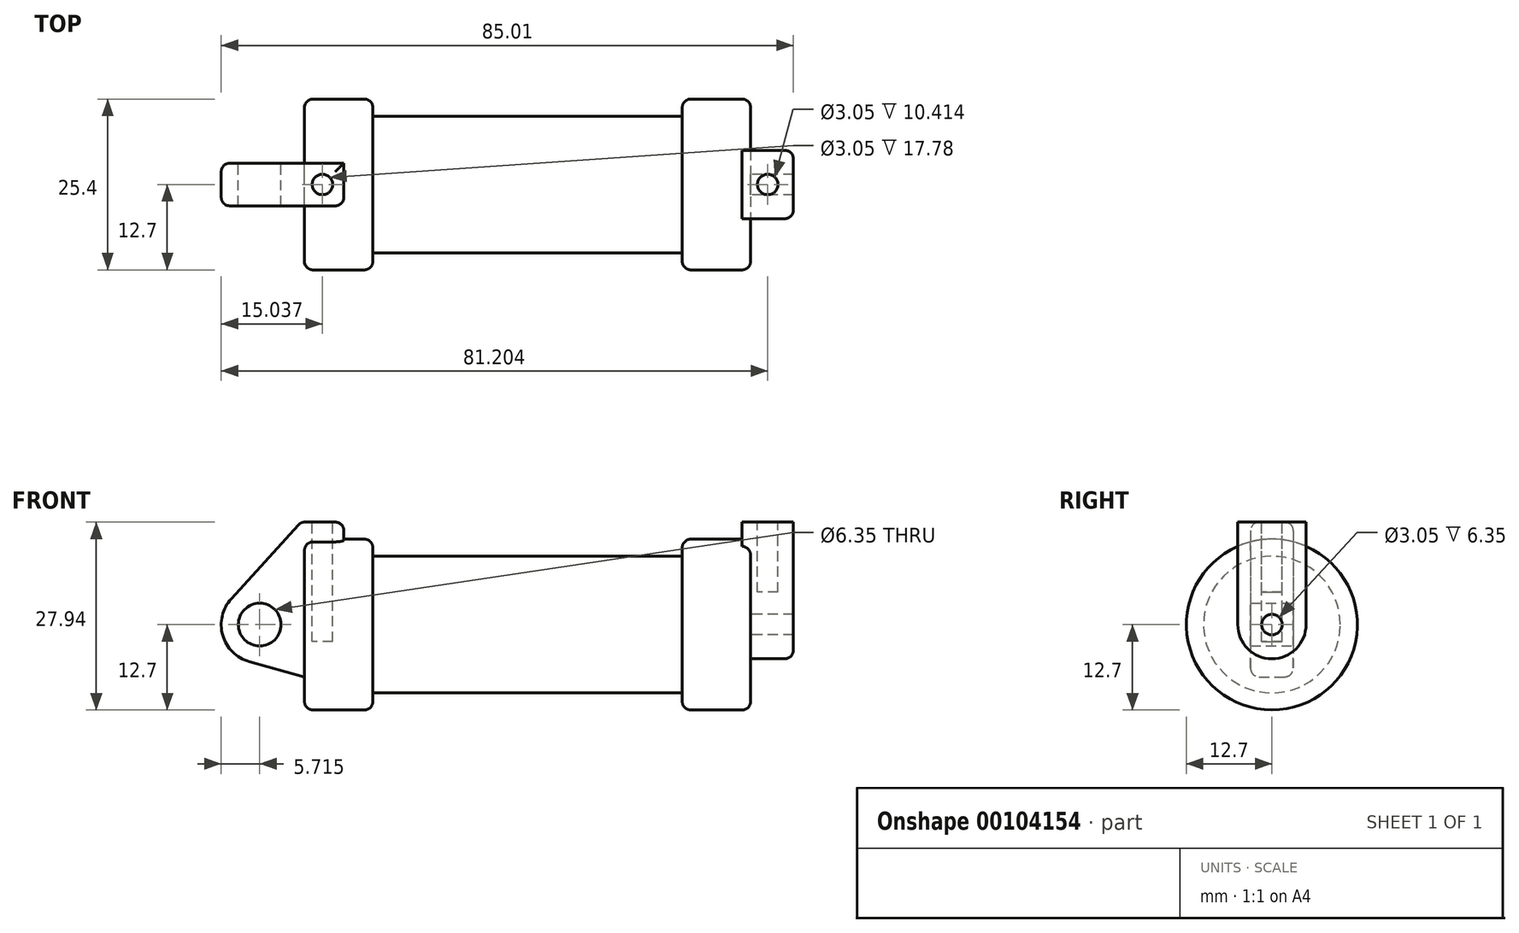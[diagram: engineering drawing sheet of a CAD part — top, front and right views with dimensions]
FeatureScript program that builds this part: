
annotation { "Feature Type Name" : "Feature", "Feature Type Description" : "" }
export const myFeature = defineFeature(function(context is Context, id is Id, definition is map)
    precondition{}
    {
        {
            var Q0;
            Q0=qCreatedBy(makeId("Front.planeOp"),FACE);
            var sketch = newSketch(context, id + "F0", { "sketchPlane" : qUnion([Q0])});
            skLineSegment(sketch, "E0", {"start": v(0, 0) * mm, "end": v(0, 12.7) * mm});
            skLineSegment(sketch, "E1", {"start": v(0, 12.7) * mm, "end": v(10.16, 12.7) * mm});
            skLineSegment(sketch, "E2", {"start": v(10.16, 12.7) * mm, "end": v(10.16, 10.16) * mm});
            skLineSegment(sketch, "E3", {"start": v(10.16, 10.16) * mm, "end": v(56.13, 10.16) * mm});
            skLineSegment(sketch, "E4", {"start": v(56.13, 10.16) * mm, "end": v(56.13, 12.7) * mm});
            skLineSegment(sketch, "E5", {"start": v(56.13, 12.7) * mm, "end": v(66.3, 12.7) * mm});
            skLineSegment(sketch, "E6", {"start": v(66.3, 12.7) * mm, "end": v(66.3, 0) * mm});
            skLineSegment(sketch, "E7", {"start": v(66.3, 0) * mm, "end": v(0, 0) * mm});
            skLineSegment(sketch, "E8", {"start": v(5.84, 15.24) * mm, "end": v(-0.5, 15.24) * mm});
            skLineSegment(sketch, "E9", {"start": v(-0.5, 15.24) * mm, "end": v(-10.88, 3.85) * mm});
            skLineSegment(sketch, "E10", {"start": v(0, 0) * mm, "end": v(-6.65, 0) * mm});
            skCircle(sketch, "E11", {"center": v(-6.65, 0) * mm, "radius": 5.72 * mm});
            skCircle(sketch, "E12", {"center": v(-6.65, 0) * mm, "radius": 3.18 * mm});
            skLineSegment(sketch, "E13", {"start": v(5.84, 15.24) * mm, "end": v(5.84, -9.4) * mm});
            skLineSegment(sketch, "E14", {"start": v(5.84, -9.4) * mm, "end": v(-8.18, -5.5) * mm});
            skSolve(sketch);
        }
        {
            var Q0;
            {var subQ0=sQuery(id+"F0.wireOp",EDGE,"E2");Q0=makeQuery(id+"F0.imprint","IMPRINT",FACE,{"disambiguationData":[TD([[makeQuery(id+"F0.imprint","IMPRINT",EDGE,{"derivedFrom":subQ0}),-1.0]])]});}
            var Q1;
            Q1=sQuery(id+"F0.wireOp",EDGE,"E7");
            revolve(context, id + "F1", {"entities" : qUnion([Q0]), "axis" : qUnion([Q1]), "revolveType" : RevolveType.FULL});
        }
        {
            var Q0;
            {var subQ0=sQuery(id+"F0.wireOp",EDGE,"E0");Q0=makeQuery(id+"F0.imprint","IMPRINT",FACE,{"disambiguationData":[TD([[makeQuery(id+"F0.imprint","IMPRINT",EDGE,{"derivedFrom":subQ0}),-1.0]])]});}
            var Q1;
            Q1=sQuery(id+"F0.wireOp",EDGE,"E7");
            revolve(context, id + "F2", {"operationType" : NewBodyOperationType.ADD, "entities" : qUnion([Q0]), "axis" : qUnion([Q1]), "revolveType" : RevolveType.FULL});
        }
        {
            var Q0;
            {var subQ3=sQuery(id+"F0.wireOp",EDGE,"E0");Q0=makeQuery(id+"F0.imprint","IMPRINT",FACE,{"disambiguationData":[TD([[makeQuery(id+"F0.imprint","IMPRINT",EDGE,{"derivedFrom":subQ3}),1.0]])]});}
            var Q1;
            {var subQ4=sQuery(id+"F0.wireOp",EDGE,"E12");Q1=makeQuery(id+"F0.imprint","IMPRINT",FACE,{"disambiguationData":[TD([[makeQuery(id+"F0.imprint","IMPRINT",EDGE,{"derivedFrom":subQ4}),-1.0]])]});}
            var Q2;
            {var subQ0=sQuery(id+"F0.wireOp",EDGE,"E14");Q2=makeQuery(id+"F0.imprint","IMPRINT",FACE,{"disambiguationData":[TD([[makeQuery(id+"F0.imprint","IMPRINT",EDGE,{"derivedFrom":subQ0}),-1.0]])]});}
            var Q3;
            {var subQ0=sQuery(id+"F0.wireOp",EDGE,"E0");Q3=makeQuery(id+"F0.imprint","IMPRINT",FACE,{"disambiguationData":[TD([[makeQuery(id+"F0.imprint","IMPRINT",EDGE,{"derivedFrom":subQ0}),-1.0]])]});}
            extrude(context, id + "F3", {"entities" : qUnion([Q0, Q1, Q2, Q3]), "operationType" : NewBodyOperationType.ADD, "endBound" : BoundingType.SYMMETRIC, "depth" : 6.35 * mm});
        }
        {
            var Q0;
            Q0=makeQuery(id+"F1.opRevolve","SWEPT_FACE",FACE,{"disambiguationData":[OSD([sQuery(id+"F0.wireOp",EDGE,"E6")])]});
            var sketch = newSketch(context, id + "F4", { "sketchPlane" : qUnion([Q0])});
            skCircle(sketch, "E15", {"center": v(0, 0) * mm, "radius": 1.52 * mm});
            skCircle(sketch, "E16", {"center": v(0, 0) * mm, "radius": 5.08 * mm});
            skLineSegment(sketch, "E17", {"start": v(5.08, 0) * mm, "end": v(5.08, 15.24) * mm});
            skLineSegment(sketch, "E18", {"start": v(-5.08, 0) * mm, "end": v(-5.08, 15.24) * mm});
            skLineSegment(sketch, "E19", {"start": v(-5.08, 15.24) * mm, "end": v(5.08, 15.24) * mm});
            skSolve(sketch);
        }
        {
            var Q0;
            Q0=makeQuery(id+"F4.imprint","IMPRINT",FACE,{"disambiguationData":[TD([[makeQuery(id+"F4.imprint","IMPRINT",EDGE,{"derivedFrom":sQuery(id+"F4.wireOp",EDGE,"E15")}),-1.0]])]});
            var Q1;
            {var subQ0=sQuery(id+"F4.wireOp",EDGE,"E17");var subQ1=sQuery(id+"F4.wireOp",EDGE,"E16");var subQ2=makeQuery(id+"F4.imprint","INTERSECT",VERTEX,{"derivedFrom":[subQ1,subQ0]});Q1=makeQuery(id+"F4.imprint","IMPRINT",FACE,{"disambiguationData":[TD([[makeQuery(id+"F4.imprint","IMPRINT",EDGE,{"disambiguationData":[TD([[subQ2,-1.0]])],"derivedFrom":subQ1}),-1.0]])]});}
            var Q2;
            {var subQ0=sQuery(id+"F4.wireOp",EDGE,"E19");Q2=makeQuery(id+"F4.imprint","IMPRINT",FACE,{"disambiguationData":[TD([[makeQuery(id+"F4.imprint","IMPRINT",EDGE,{"derivedFrom":subQ0}),-1.0]])]});}
            extrude(context, id + "F5", {"entities" : qUnion([Q0, Q1, Q2]), "operationType" : NewBodyOperationType.ADD, "depth" : 6.35 * mm, "hasSecondDirection" : true, "secondDirectionOppositeDirection" : true, "secondDirectionDepth" : 1.27 * mm});
        }
        {
            var Q0;
            Q0=makeQuery(id+"F5.opExtrude","SWEPT_FACE",FACE,{"disambiguationData":[OSD([sQuery(id+"F4.wireOp",EDGE,"E19")])]});
            var sketch = newSketch(context, id + "F6", { "sketchPlane" : qUnion([Q0])});
            skCircle(sketch, "E20", {"center": v(68.83, 0) * mm, "radius": 1.52 * mm});
            skSolve(sketch);
        }
        {
            var Q0;
            Q0=makeQuery(id+"F6.imprint","IMPRINT",FACE,{"disambiguationData":[TD([[makeQuery(id+"F6.imprint","IMPRINT",EDGE,{"derivedFrom":sQuery(id+"F6.wireOp",EDGE,"E20")}),1.0]])]});
            extrude(context, id + "F7", {"entities" : qUnion([Q0]), "operationType" : NewBodyOperationType.REMOVE, "oppositeDirection" : true, "depth" : 10.4 * mm});
        }
        {
            var Q0;
            Q0=makeQuery(id+"F3.opExtrude","SWEPT_FACE",FACE,{"disambiguationData":[OSD([sQuery(id+"F0.wireOp",EDGE,"E8")])]});
            var sketch = newSketch(context, id + "F8", { "sketchPlane" : qUnion([Q0])});
            skCircle(sketch, "E21", {"center": v(2.67, 0) * mm, "radius": 1.52 * mm});
            skPoint(sketch, "E21.centerSnap0", {"position": v(5.84, 0) * mm});
            skSolve(sketch);
        }
        {
            var Q0;
            Q0=makeQuery(id+"F8.imprint","IMPRINT",FACE,{"disambiguationData":[TD([[makeQuery(id+"F8.imprint","IMPRINT",EDGE,{"derivedFrom":sQuery(id+"F8.wireOp",EDGE,"E21")}),1.0]])]});
            extrude(context, id + "F9", {"entities" : qUnion([Q0]), "operationType" : NewBodyOperationType.REMOVE, "oppositeDirection" : true, "depth" : 17.78 * mm});
        }
        {
            var Q0;
            Q0=makeQuery(id+"F1.opRevolve","SWEPT_EDGE",EDGE,{"disambiguationData":[OSD([sQuery(id+"F0.wireOp",EDGE,"E5"),sQuery(id+"F0.wireOp",EDGE,"E6")])]});
            var Q1;
            Q1=makeQuery(id+"F1.opRevolve","SWEPT_EDGE",EDGE,{"disambiguationData":[OSD([sQuery(id+"F0.wireOp",EDGE,"E4"),sQuery(id+"F0.wireOp",EDGE,"E5")])]});
            var Q2;
            Q2=makeQuery(id+"F1.opRevolve","SWEPT_EDGE",EDGE,{"disambiguationData":[OSD([sQuery(id+"F0.wireOp",EDGE,"E1"),sQuery(id+"F0.wireOp",EDGE,"E2")])]});
            var Q3;
            Q3=makeQuery(id+"F2.opRevolve","SWEPT_EDGE",EDGE,{"disambiguationData":[OSD([sQuery(id+"F0.wireOp",EDGE,"E0"),sQuery(id+"F0.wireOp",EDGE,"E1")])]});
            fillet(context, id + "F10", {"entities" : qUnion([Q0, Q1, Q2, Q3]), "radius" : 1.27 * mm, "tangentPropagation" : true, "allowEdgeOverflow" : false});
        }
        {
            var Q0;
            Q0=makeQuery(id+"F5.opExtrude","CAP_EDGE",EDGE,{"disambiguationData":[OSD([sQuery(id+"F4.wireOp",EDGE,"E18")])],"isStart":false});
            fillet(context, id + "F11", {"entities" : qUnion([Q0]), "radius" : 1.27 * mm, "tangentPropagation" : true, "allowEdgeOverflow" : false});
        }
        {
            var Q0;
            Q0=makeQuery(id+"F3.opExtrude","CAP_EDGE",EDGE,{"disambiguationData":[OSD([sQuery(id+"F0.wireOp",EDGE,"E11")])],"isStart":false});
            var Q1;
            Q1=makeQuery(id+"F3.opExtrude","CAP_EDGE",EDGE,{"disambiguationData":[OSD([sQuery(id+"F0.wireOp",EDGE,"E9")])],"isStart":false});
            var Q2;
            Q2=makeQuery(id+"F3.opExtrude","CAP_EDGE",EDGE,{"disambiguationData":[OSD([sQuery(id+"F0.wireOp",EDGE,"E8")])],"isStart":false});
            var Q3;
            Q3=makeQuery(id+"F3.opExtrude","CAP_EDGE",EDGE,{"disambiguationData":[OSD([sQuery(id+"F0.wireOp",EDGE,"E13")])],"isStart":false});
            var Q4;
            Q4=makeQuery(id+"F3.opExtrude","CAP_EDGE",EDGE,{"disambiguationData":[OSD([sQuery(id+"F0.wireOp",EDGE,"E14")])],"isStart":false});
            var Q5;
            Q5=makeQuery(id+"F3.opExtrude","CAP_EDGE",EDGE,{"disambiguationData":[OSD([sQuery(id+"F0.wireOp",EDGE,"E11")])],"isStart":true});
            var Q6;
            Q6=makeQuery(id+"F3.opExtrude","CAP_EDGE",EDGE,{"disambiguationData":[OSD([sQuery(id+"F0.wireOp",EDGE,"E9")])],"isStart":true});
            var Q7;
            Q7=makeQuery(id+"F3.opExtrude","CAP_EDGE",EDGE,{"disambiguationData":[OSD([sQuery(id+"F0.wireOp",EDGE,"E8")])],"isStart":true});
            var Q8;
            Q8=makeQuery(id+"F3.opExtrude","SWEPT_EDGE",EDGE,{"disambiguationData":[OSD([sQuery(id+"F0.wireOp",EDGE,"E8"),sQuery(id+"F0.wireOp",EDGE,"E13")])]});
            var Q9;
            Q9=makeQuery(id+"F3.opExtrude","SWEPT_EDGE",EDGE,{"disambiguationData":[OSD([sQuery(id+"F0.wireOp",EDGE,"E8"),sQuery(id+"F0.wireOp",EDGE,"E9")])]});
            var Q10;
            Q10=makeQuery(id+"F3.opExtrude","CAP_EDGE",EDGE,{"disambiguationData":[OSD([sQuery(id+"F0.wireOp",EDGE,"E14")])],"isStart":true});
            fillet(context, id + "F12", {"entities" : qUnion([Q0, Q1, Q2, Q3, Q4, Q5, Q6, Q7, Q8, Q9, Q10]), "radius" : 1.27 * mm, "tangentPropagation" : true, "allowEdgeOverflow" : false});
        }
    });
